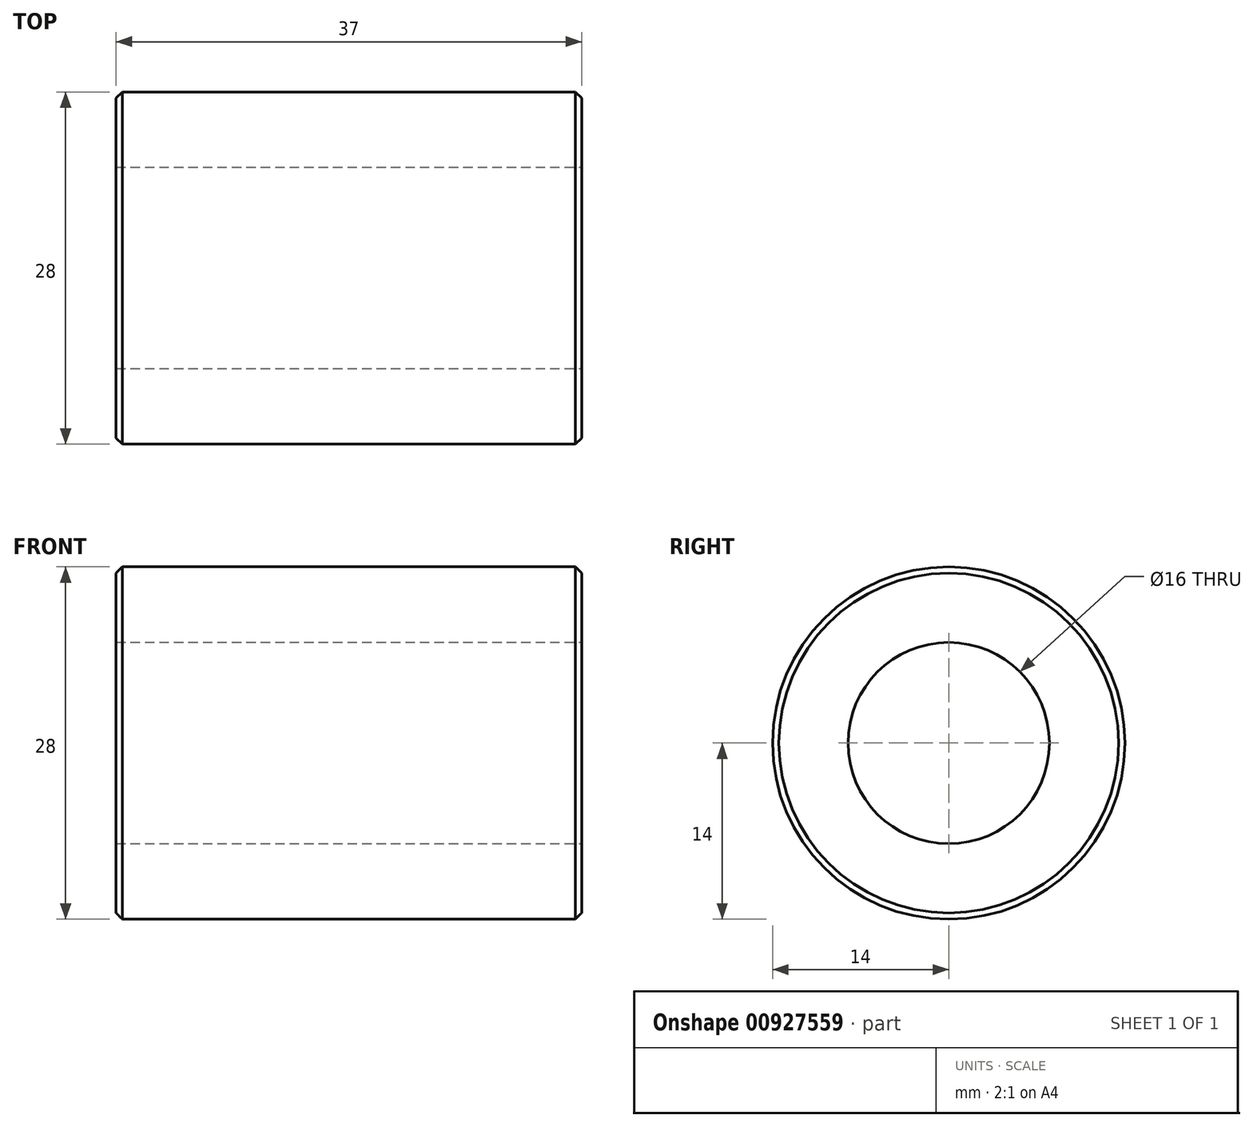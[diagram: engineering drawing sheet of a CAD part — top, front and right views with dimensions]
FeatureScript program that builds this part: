
annotation { "Feature Type Name" : "Feature", "Feature Type Description" : "" }
export const myFeature = defineFeature(function(context is Context, id is Id, definition is map)
    precondition{}
    {
        {
            var Q0;
            Q0=qCreatedBy(makeId("Right.planeOp"),FACE);
            var sketch = newSketch(context, id + "F0", { "sketchPlane" : qUnion([Q0])});
            skCircle(sketch, "E0", {"center": v(0, 0) * mm, "radius": 8 * mm});
            skCircle(sketch, "E1", {"center": v(0, 0) * mm, "radius": 14 * mm});
            skSolve(sketch);
        }
        {
            var Q0;
            Q0 = qSketchRegion(id + "F0", true);
            extrude(context, id + "F1", {"entities" : qUnion([Q0]), "oppositeDirection" : true, "depth" : 37 * mm, "offsetDistance" : 25 * mm});
        }
        {
            var Q0;
            Q0=makeQuery(id+"F1.opExtrude","CAP_EDGE",EDGE,{"disambiguationData":[OSD([sQuery(id+"F0.wireOp",EDGE,"E1")])],"isStart":true});
            var Q1;
            Q1=makeQuery(id+"F1.opExtrude","CAP_EDGE",EDGE,{"disambiguationData":[OSD([sQuery(id+"F0.wireOp",EDGE,"E1")])],"isStart":false});
            chamfer(context, id + "F2", {"entities" : qUnion([Q0, Q1]), "width" : 0.5 * mm, "tangentPropagation" : true});
        }
    });
